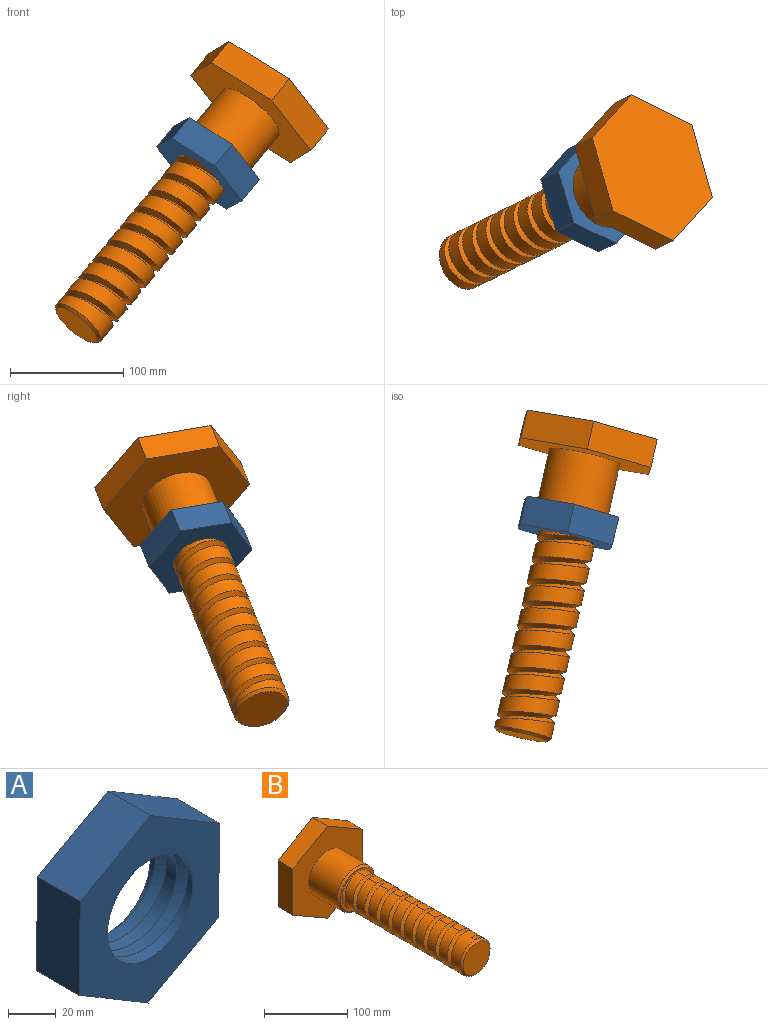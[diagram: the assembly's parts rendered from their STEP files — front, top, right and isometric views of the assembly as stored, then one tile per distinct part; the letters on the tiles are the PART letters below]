
ASSEMBLY  parts=2 mates=1
PART A: 12 faces, bbox 83.8x30.2x95.9 mm
  f0: cylinder r=25.4mm len=50.8mm, axis (0,1,0), area 2280.6mm2, adj f1,f8,f9,f10,f11
  f1: plane 95.89x83.79mm, normal (0,1,0), area 3711.8mm2, adj f0,f2,f3,f4,f5,f6,f7,f9
  f2: plane 47.94x25.4mm, normal (1,0,-0.02), area 1217.9mm2, adj f1,f3,f7,f8
  f3: plane 41.14x25.4mm, normal (0.51,0,0.86), area 1217.9mm2, adj f1,f2,f4,f8
  f4: plane 41.9x25.4mm, normal (-0.49,0,0.87), area 1217.9mm2, adj f1,f3,f5,f8
  f5: plane 47.94x25.4mm, normal (-1,0,0.02), area 1217.9mm2, adj f1,f4,f6,f8
  f6: plane 41.14x25.4mm, normal (-0.51,0,-0.86), area 1217.9mm2, adj f1,f5,f7,f8
  f7: plane 41.9x25.4mm, normal (0.49,0,-0.87), area 1217.9mm2, adj f1,f2,f6,f8
  f8: plane 95.89x83.79mm, normal (0,-1,0), area 3946.6mm2, adj f0,f2,f3,f4,f5,f6,f7
  f9: bspline ~63.14x63.14mm, area 2097.5mm2, adj f0,f1,f10,f11
  f10: bspline ~63.14x63.14mm, area 1833.8mm2, adj f0,f1,f9,f11
  f11: plane 6.35x5.5mm, normal (1,0,0), area 17.5mm2, adj f0,f9,f10
PART B: 28 faces, bbox 117.5x279.4x135.7 mm
  f0: plane 58.76x33.92mm, normal (0.5,0,0.87), area 1723.3mm2, adj f1,f5,f6,f7
  f1: plane 58.76x33.92mm, normal (-0.5,0,0.87), area 1723.3mm2, adj f0,f2,f6,f7
  f2: plane 67.85x25.4mm, normal (-1,0,0), area 1723.3mm2, adj f1,f3,f6,f7
  f3: plane 58.76x33.92mm, normal (-0.5,0,-0.87), area 1723.3mm2, adj f2,f4,f6,f7
  f4: plane 58.76x33.92mm, normal (0.5,0,-0.87), area 1723.3mm2, adj f3,f5,f6,f7
  f5: plane 67.85x25.4mm, normal (1,0,0), area 1723.3mm2, adj f0,f4,f6,f7
  f6: plane 135.69x117.51mm, normal (0,-1,0), area 8792.6mm2, adj f0,f1,f2,f3,f4,f5,f8
  f7: plane 135.69x117.51mm, normal (0,1,0), area 11959.5mm2, adj f0,f1,f2,f3,f4,f5
  f8: cylinder r=31.75mm len=63.5mm, axis (0,1,0), area 9627.4mm2, adj f6,f10
  f9: plane 58.42x58.42mm, normal (0,-1,0), area 653.7mm2, adj f10,f12,f27
  f10: cone r=29.21mm half-angle=45deg, axis (0,1,0), area 687.9mm2, adj f8,f9
  f11: cylinder r=25.4mm len=50.8mm, axis (0,1,0), area 3792.1mm2, adj f20,f22,f24,f25,f26
  f12: cylinder r=25.4mm len=50.8mm, axis (0,1,0), area 747.9mm2, adj f9,f13,f25
  f13: cylinder r=25.4mm len=50.8mm, axis (0,1,0), area 2188.9mm2, adj f12,f14,f25,f26
  f14: cylinder r=25.4mm len=50.8mm, axis (0,1,0), area 2189.2mm2, adj f13,f15,f25,f26
  f15: cylinder r=25.4mm len=50.8mm, axis (0,1,0), area 2189.2mm2, adj f14,f16,f25,f26
  f16: cylinder r=25.4mm len=50.8mm, axis (0,1,0), area 2189mm2, adj f15,f17,f25,f26
  f17: cylinder r=25.4mm len=50.8mm, axis (0,1,0), area 2188.7mm2, adj f16,f18,f25,f26
  f18: cylinder r=25.4mm len=50.8mm, axis (0,1,0), area 2188.8mm2, adj f17,f19,f25,f26
  f19: cylinder r=25.4mm len=50.8mm, axis (0,1,0), area 2189.1mm2, adj f18,f20,f25,f26
  f20: cylinder r=25.4mm len=50.8mm, axis (0,1,0), area 2189.2mm2, adj f11,f19,f25,f26
  f21: plane 45.72x45.72mm, normal (0,-1,0), area 1641.7mm2, adj f22
  f22: cone r=22.86mm half-angle=45deg, axis (0,1,0), area 544.6mm2, adj f11,f21
  f23: plane 6.35x5.5mm, normal (-1,0,0), area 17.5mm2, adj f25,f26,f27
  f24: plane 6.35x5.5mm, normal (1,0,0), area 17.5mm2, adj f11,f25,f26
  f25: bspline ~203.84x53.41mm, area 9115.5mm2, adj f11,f12,f13,f14,f15,f16,f17,f18
  f26: bspline ~203.84x53.41mm, area 9091.7mm2, adj f11,f13,f14,f15,f16,f17,f18,f19
  f27: cylinder r=25.4mm len=35.68mm, axis (0,-1,0), area 162.6mm2, adj f9,f23,f25,f26
PLACE A rot(axis=(0.67,-0.17,-0.72),73.8deg) t=(169.84,-366.82,-127.1)mm
PLACE B rot(axis=(0.43,0.8,0.41),168.4deg) t=(215.61,-347.11,-72.79)mm
MATE cylindrical B.f8 <-> A.f1  axis (0.61,0.3,0.74) through (170.84,-369.12,-126.99)mm
